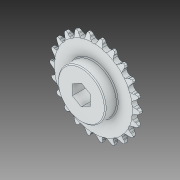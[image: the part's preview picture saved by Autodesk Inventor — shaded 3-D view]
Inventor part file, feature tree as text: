
AUTODESK INVENTOR PART (.ipt)
format: ipt  version: 2019 (Build 230136000, 136)  size: 617,472 bytes
history: native  units: in
note: dims shown in document units (in); Inventor stores cm internally (conversion verified against a paired STEP export)
features: chamfer x1
ambient origin geometry x8: Origin, YZ Plane, XZ Plane, XY Plane, X Axis, Y Axis, Z Axis, Center Point
bodies: Solid1 (feature_tree)
feature tree (1):
  chamfer  "Chamfer2"  [1 undecoded]
note: 1 required parameter value undecoded (feature->parameter linkage not recoverable at this tier; creation-order binding heuristic only, values carry confidence <= 0.55)
